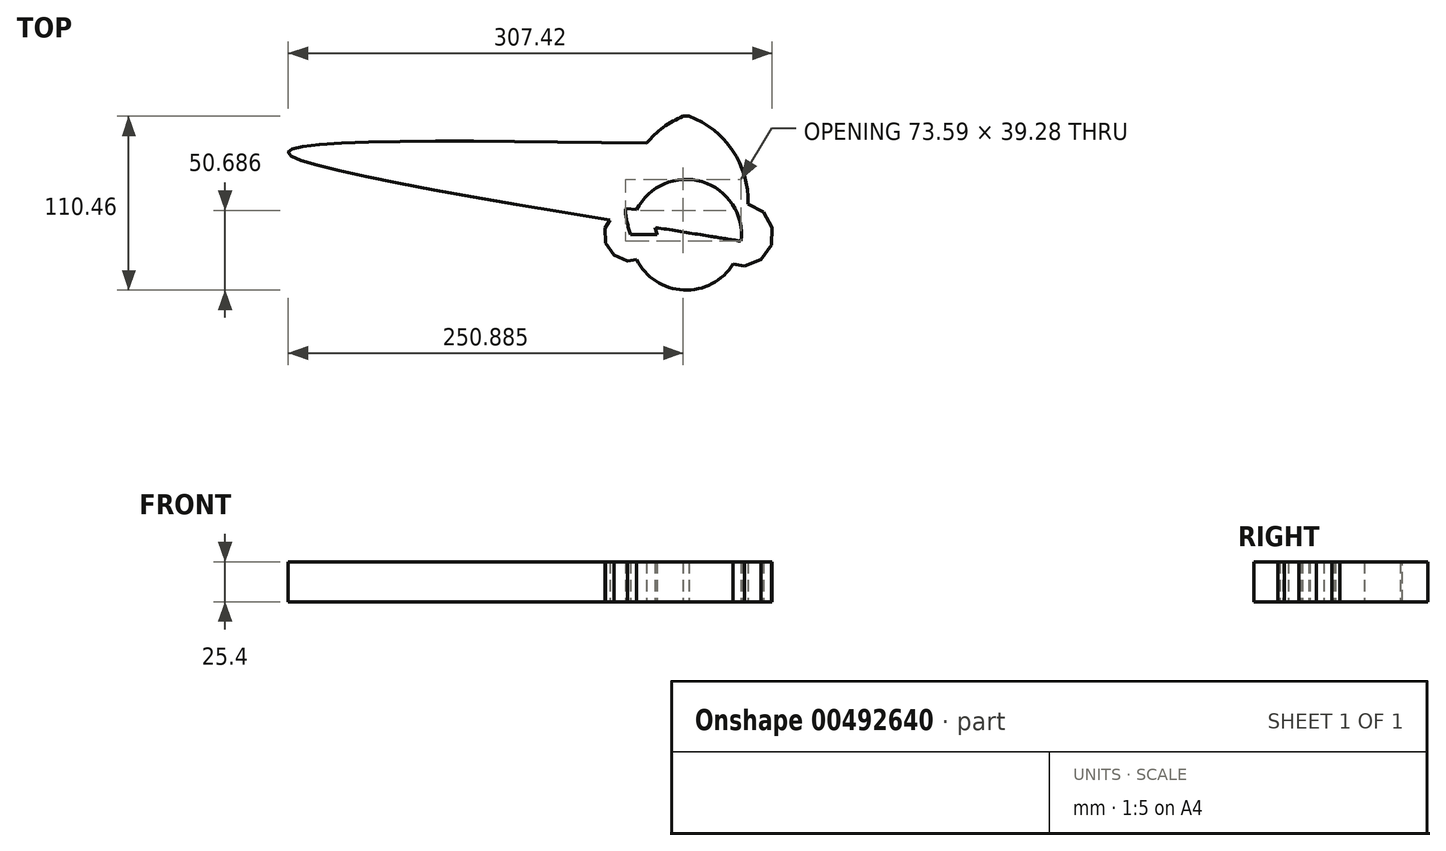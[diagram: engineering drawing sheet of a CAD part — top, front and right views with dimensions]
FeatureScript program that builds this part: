
annotation { "Feature Type Name" : "Feature", "Feature Type Description" : "" }
export const myFeature = defineFeature(function(context is Context, id is Id, definition is map)
    precondition{}
    {
        {
            var Q0;
            Q0=qCreatedBy(makeId("Top.planeOp"),FACE);
            var sketch = newSketch(context, id + "F0", { "sketchPlane" : qUnion([Q0])});
            skCircle(sketch, "E0", {"center": v(0, 0) * mm, "radius": 35.2 * mm});
            skLineSegment(sketch, "E1", {"start": v(0, 0) * mm, "end": v(35.2, 0) * mm});
            skLineSegment(sketch, "E2", {"start": v(0, 0) * mm, "end": v(-35.2, 0) * mm});
            skArc(sketch, "E3", {"start": v(0, 75.92) * mm, "mid": v(-33.27, 45.23) * mm, "end": v(-35.2, 0) * mm});
            skArc(sketch, "E4", {"start": v(35.2, 0) * mm, "mid": v(34, 45.56) * mm, "end": v(0, 75.92) * mm});
            skCircle(sketch, "E5.cCircle", {"center": v(-35.2, 0) * mm, "radius": 16.16 * mm, "construction": true});
            skLineSegment(sketch, "E5.0", {"start": v(-51.49, 4.26) * mm, "end": v(-46.6, 12.4) * mm});
            skLineSegment(sketch, "E5.1", {"start": v(-46.6, 12.4) * mm, "end": v(-38.08, 16.6) * mm});
            skLineSegment(sketch, "E5.2", {"start": v(-38.08, 16.6) * mm, "end": v(-28.65, 15.52) * mm});
            skLineSegment(sketch, "E5.3", {"start": v(-28.65, 15.52) * mm, "end": v(-21.3, 9.52) * mm});
            skLineSegment(sketch, "E5.4", {"start": v(-21.3, 9.52) * mm, "end": v(-18.35, 0.5) * mm});
            skLineSegment(sketch, "E5.5", {"start": v(-18.35, 0.5) * mm, "end": v(-20.76, -8.68) * mm});
            skLineSegment(sketch, "E5.6", {"start": v(-20.76, -8.68) * mm, "end": v(-27.74, -15.1) * mm});
            skLineSegment(sketch, "E5.7", {"start": v(-27.74, -15.1) * mm, "end": v(-37.1, -16.74) * mm});
            skLineSegment(sketch, "E5.8", {"start": v(-37.1, -16.74) * mm, "end": v(-45.84, -13.05) * mm});
            skLineSegment(sketch, "E5.9", {"start": v(-45.84, -13.05) * mm, "end": v(-51.2, -5.22) * mm});
            skLineSegment(sketch, "E5.10", {"start": v(-51.2, -5.22) * mm, "end": v(-51.49, 4.26) * mm});
            skPoint(sketch, "E5.0.midPoint", {"position": v(-49.04, 8.33) * mm});
            skCircle(sketch, "E6.cCircle", {"center": v(35.2, 0) * mm, "radius": 19.24 * mm, "construction": true});
            skLineSegment(sketch, "E6.0", {"start": v(49.06, 14.49) * mm, "end": v(54.69, 4.7) * mm});
            skLineSegment(sketch, "E6.1", {"start": v(54.69, 4.7) * mm, "end": v(54.13, -6.6) * mm});
            skLineSegment(sketch, "E6.2", {"start": v(54.13, -6.6) * mm, "end": v(47.56, -15.79) * mm});
            skLineSegment(sketch, "E6.3", {"start": v(47.56, -15.79) * mm, "end": v(37.06, -19.96) * mm});
            skLineSegment(sketch, "E6.4", {"start": v(37.06, -19.96) * mm, "end": v(25.97, -17.8) * mm});
            skLineSegment(sketch, "E6.5", {"start": v(25.97, -17.8) * mm, "end": v(17.8, -10) * mm});
            skLineSegment(sketch, "E6.6", {"start": v(17.8, -10) * mm, "end": v(15.17, 1) * mm});
            skLineSegment(sketch, "E6.7", {"start": v(15.17, 1) * mm, "end": v(18.88, 11.66) * mm});
            skLineSegment(sketch, "E6.8", {"start": v(18.88, 11.66) * mm, "end": v(27.78, 18.63) * mm});
            skLineSegment(sketch, "E6.9", {"start": v(27.78, 18.63) * mm, "end": v(39.02, 19.68) * mm});
            skLineSegment(sketch, "E6.10", {"start": v(39.02, 19.68) * mm, "end": v(49.06, 14.49) * mm});
            skPoint(sketch, "E6.0.midPoint", {"position": v(51.87, 9.59) * mm});
            skFitSpline(sketch, "E7", {"points": [v(55.7, -7.46) * mm, v(-252.72, 52.4) * mm, v(-14.32, 57.98) * mm], "startDerivative": vector(-868.18, 138.75) * mm, "endDerivative": vector(765.6, -11.32) * mm});
            skSolve(sketch);
        }
        {
            var Q0;
            {var subQ0=sQuery(id+"F0.wireOp",EDGE,"E1");Q0=makeQuery(id+"F0.imprint","IMPRINT",FACE,{"disambiguationData":[TD([[makeQuery(id+"F0.imprint","IMPRINT",EDGE,{"derivedFrom":subQ0}),1.0]])]});}
            extrude(context, id + "F1", {"entities" : qUnion([Q0]), "depth" : 25.4 * mm});
        }
        {
            var Q0;
            Q0 = qSketchRegion(id + "F0", true);
            extrude(context, id + "F2", {"entities" : qUnion([Q0]), "operationType" : NewBodyOperationType.ADD, "depth" : 25.4 * mm});
        }
        {
            var Q0;
            Q0=makeQuery(id+"F1.opExtrude","SWEPT_FACE",FACE,{"disambiguationData":[OSD([sQuery(id+"F0.wireOp",EDGE,"E6.8")])]});
            var Q1;
            Q1=makeQuery(id+"F2.opExtrude","SWEPT_EDGE",EDGE,{"disambiguationData":[OSD([sQuery(id+"F0.wireOp",EDGE,"E3"),sQuery(id+"F0.wireOp",EDGE,"E4")])]});
            chamfer(context, id + "F3", {"entities" : qUnion([Q0, Q1]), "width" : 5.08 * mm, "tangentPropagation" : true});
        }
    });
